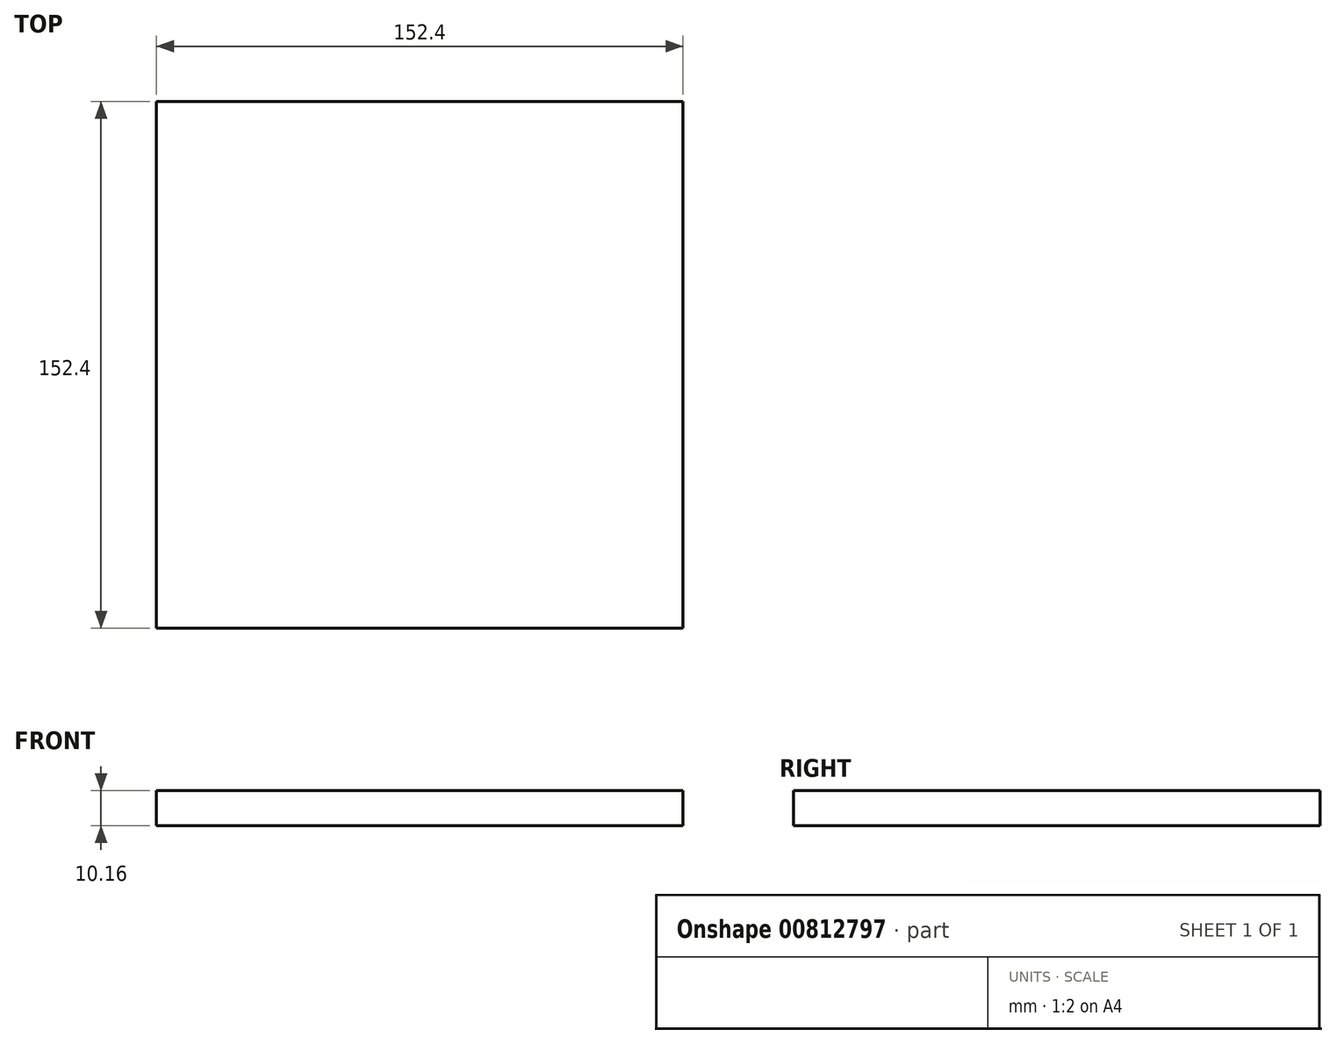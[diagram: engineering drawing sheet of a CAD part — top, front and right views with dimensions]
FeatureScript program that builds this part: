
annotation { "Feature Type Name" : "Feature", "Feature Type Description" : "" }
export const myFeature = defineFeature(function(context is Context, id is Id, definition is map)
    precondition{}
    {
        {
            var Q0;
            Q0=qCreatedBy(makeId("Top.planeOp"),FACE);
            var sketch = newSketch(context, id + "F0", { "sketchPlane" : qUnion([Q0])});
            skLineSegment(sketch, "E0.bottom", {"start": v(0, 0) * mm, "end": v(-152.4, 0) * mm});
            skLineSegment(sketch, "E0.top", {"start": v(0, -152.4) * mm, "end": v(-152.4, -152.4) * mm});
            skLineSegment(sketch, "E0.left", {"start": v(0, 0) * mm, "end": v(0, -152.4) * mm});
            skLineSegment(sketch, "E0.right", {"start": v(-152.4, 0) * mm, "end": v(-152.4, -152.4) * mm});
            skSolve(sketch);
        }
        {
            var Q0;
            Q0=makeQuery(id+"F0.imprint","IMPRINT",FACE,{"disambiguationData":[TD([[makeQuery(id+"F0.imprint","IMPRINT",EDGE,{"derivedFrom":sQuery(id+"F0.wireOp",EDGE,"E0.bottom")}),1.0]])]});
            var sketch = newSketch(context, id + "F1", { "sketchPlane" : qUnion([Q0])});
            skSolve(sketch);
        }
        {
            var Q0;
            Q0=makeQuery(id+"F1.imprint","IMPRINT",FACE,{"disambiguationData":[TD([[makeQuery(id+"F1.imprint","IMPRINT",EDGE,{"derivedFrom":makeQuery(id+"F0.imprint","IMPRINT",EDGE,{"derivedFrom":sQuery(id+"F0.wireOp",EDGE,"E0.bottom")})}),1.0]])]});
            var sketch = newSketch(context, id + "F2", { "sketchPlane" : qUnion([Q0])});
            skText(sketch, "E1", { "text": "A", "fontName": "OpenSans-Bold.ttf"});
            skText(sketch, "E2", { "text": "B", "fontName": "OpenSans-Bold.ttf"});
            skText(sketch, "E3", { "text": "C", "fontName": "OpenSans-Bold.ttf"});
            const initialGuessF2  = {"E1": [-0.14797, -0.02053, 1, 0, 0.01657], "E2": [-0.12625, -0.0209, 1, 0, 0.01695], "E3": [-0.10663, -0.02129, 1, 0, 0.01772]};
            skSetInitialGuess(sketch, initialGuessF2);
            skSolve(sketch);
        }
        {
            var Q0;
            Q0=makeQuery(id+"F0.imprint","IMPRINT",FACE,{"disambiguationData":[TD([[makeQuery(id+"F0.imprint","IMPRINT",EDGE,{"derivedFrom":sQuery(id+"F0.wireOp",EDGE,"E0.bottom")}),1.0]])]});
            extrude(context, id + "F3", {"entities" : qUnion([Q0]), "endBound" : BoundingType.SYMMETRIC, "depth" : 10.16 * mm, "offsetDistance" : 25.4 * mm});
        }
        {
            var Q0;
            Q0 = qSketchRegion(id + "F2", true);
            extrude(context, id + "F4", {"entities" : qUnion([Q0]), "operationType" : NewBodyOperationType.ADD, "endBound" : BoundingType.UP_TO_NEXT, "oppositeDirection" : true, "depth" : 5.08 * mm, "offsetDistance" : 25.4 * mm, "hasDraft" : true, "draftAngle" : 3 * degree});
        }
    });
